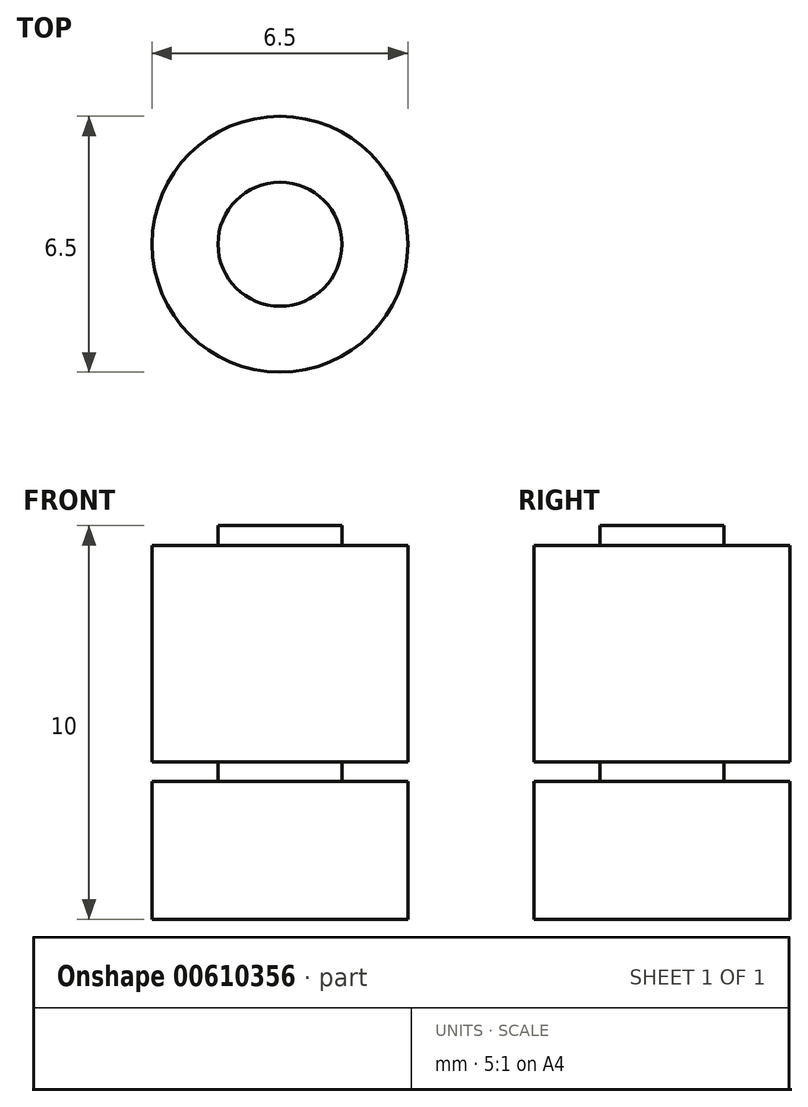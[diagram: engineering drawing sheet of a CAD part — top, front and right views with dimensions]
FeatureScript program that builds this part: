
annotation { "Feature Type Name" : "Feature", "Feature Type Description" : "" }
export const myFeature = defineFeature(function(context is Context, id is Id, definition is map)
    precondition{}
    {
        {
            var Q0;
            Q0=qCreatedBy(makeId("Top.planeOp"),FACE);
            var sketch = newSketch(context, id + "F0", { "sketchPlane" : qUnion([Q0])});
            skCircle(sketch, "E0", {"center": v(0, 0) * mm, "radius": 3.25 * mm});
            skCircle(sketch, "E1", {"center": v(0, 0) * mm, "radius": 1.57 * mm});
            skSolve(sketch);
        }
        {
            var Q0;
            Q0=makeQuery(id+"F0.imprint","IMPRINT",FACE,{"disambiguationData":[TD([[makeQuery(id+"F0.imprint","IMPRINT",EDGE,{"derivedFrom":sQuery(id+"F0.wireOp",EDGE,"E0")}),1.0]])]});
            var Q1;
            Q1=makeQuery(id+"F0.imprint","IMPRINT",FACE,{"disambiguationData":[TD([[makeQuery(id+"F0.imprint","IMPRINT",EDGE,{"derivedFrom":sQuery(id+"F0.wireOp",EDGE,"E1")}),-1.0]])]});
            extrude(context, id + "F1", {"entities" : qUnion([Q0, Q1]), "depth" : 9.5 * mm, "offsetDistance" : 25.4 * mm});
        }
        {
            var Q0;
            Q0=makeQuery(id+"F0.imprint","IMPRINT",FACE,{"disambiguationData":[TD([[makeQuery(id+"F0.imprint","IMPRINT",EDGE,{"derivedFrom":sQuery(id+"F0.wireOp",EDGE,"E1")}),1.0]])]});
            extrude(context, id + "F2", {"entities" : qUnion([Q0]), "operationType" : NewBodyOperationType.ADD, "depth" : 10 * mm, "offsetDistance" : 25.4 * mm});
        }
        {
            var Q0;
            Q0=makeQuery(id+"F0.imprint","IMPRINT",FACE,{"disambiguationData":[TD([[makeQuery(id+"F0.imprint","IMPRINT",EDGE,{"derivedFrom":sQuery(id+"F0.wireOp",EDGE,"E0")}),1.0]])]});
            extrude(context, id + "F3", {"entities" : qUnion([Q0]), "operationType" : NewBodyOperationType.REMOVE, "depth" : 4 * mm, "offsetDistance" : 25.4 * mm, "hasSecondDirection" : true, "secondDirectionOppositeDirection" : false, "secondDirectionDepth" : 3.5 * mm});
        }
    });
